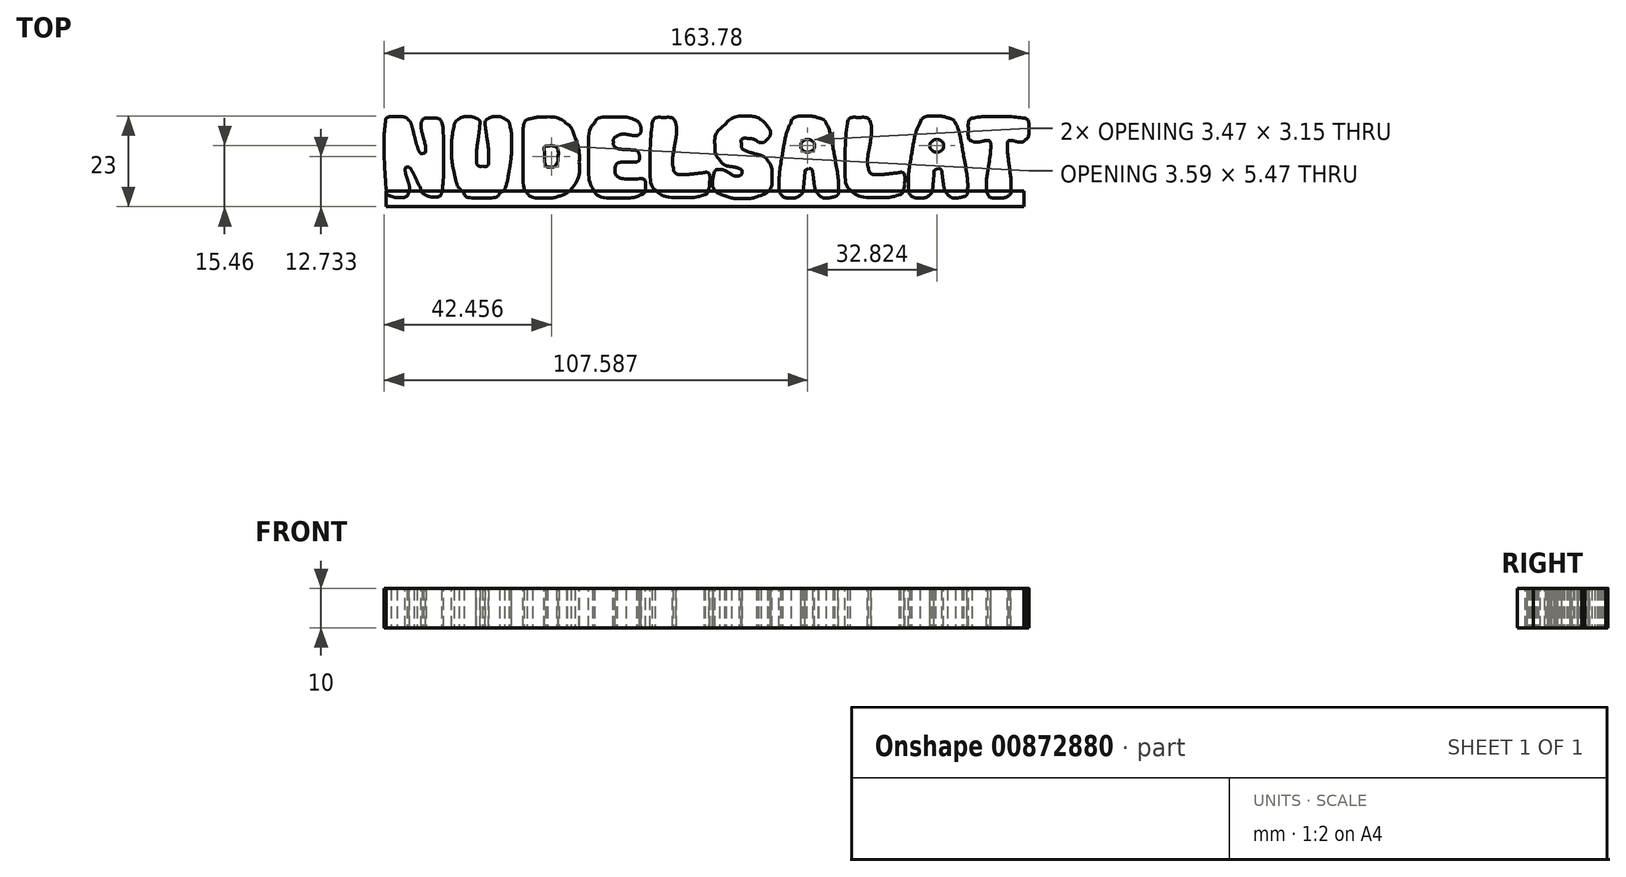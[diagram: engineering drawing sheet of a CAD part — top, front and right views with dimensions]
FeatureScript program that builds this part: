
annotation { "Feature Type Name" : "Feature", "Feature Type Description" : "" }
export const myFeature = defineFeature(function(context is Context, id is Id, definition is map)
    precondition{}
    {
        {
            var Q0;
            Q0=qCreatedBy(makeId("Top.planeOp"),FACE);
            var sketch = newSketch(context, id + "F0", { "sketchPlane" : qUnion([Q0])});
            skFitSpline(sketch, "E0", {"points": [v(-78.62, 10.37) * mm, v(-77.25, 10.37) * mm, v(-76.26, 10.07) * mm, v(-75.63, 9.46) * mm]});
            skFitSpline(sketch, "E1", {"points": [v(-75.63, 9.46) * mm, v(-75.27, 9.1) * mm, v(-74.9, 8.18) * mm, v(-74.52, 6.7) * mm]});
            skFitSpline(sketch, "E2", {"points": [v(-74.52, 6.7) * mm, v(-73.97, 4.47) * mm, v(-73.62, 3.19) * mm, v(-73.49, 2.85) * mm]});
            skFitSpline(sketch, "E3", {"points": [v(-73.49, 2.85) * mm, v(-73.03, 1.57) * mm, v(-72.51, 0.98) * mm, v(-71.92, 1.08) * mm]});
            skFitSpline(sketch, "E4", {"points": [v(-71.92, 1.08) * mm, v(-71.58, 1.13) * mm, v(-71.4, 1.47) * mm, v(-71.4, 2.08) * mm, v(-71.4, 2.78) * mm, v(-71.59, 3.82) * mm, v(-71.95, 5.18) * mm]});
            skFitSpline(sketch, "E5", {"points": [v(-71.95, 5.18) * mm, v(-72.31, 6.55) * mm, v(-72.5, 7.59) * mm, v(-72.5, 8.3) * mm, v(-72.5, 8.73) * mm, v(-72.42, 9.03) * mm, v(-72.26, 9.2) * mm]});
            skFitSpline(sketch, "E6", {"points": [v(-72.26, 9.2) * mm, v(-72.05, 9.72) * mm, v(-71.31, 9.97) * mm, v(-70.04, 9.97) * mm, v(-68.58, 9.97) * mm, v(-67.67, 9.67) * mm, v(-67.33, 9.06) * mm]});
            skFitSpline(sketch, "E7", {"points": [v(-67.33, 9.06) * mm, v(-67, 7.94) * mm, v(-66.84, 5.2) * mm, v(-66.84, 0.82) * mm, v(-66.84, -4.18) * mm, v(-67, -7.43) * mm, v(-67.33, -8.93) * mm]});
            skFitSpline(sketch, "E8", {"points": [v(-67.33, -8.93) * mm, v(-67.48, -9.65) * mm, v(-68.17, -10.02) * mm, v(-69.38, -10.02) * mm, v(-70.05, -10.02) * mm, v(-70.67, -9.87) * mm, v(-71.24, -9.59) * mm]});
            skFitSpline(sketch, "E9", {"points": [v(-71.24, -9.59) * mm, v(-71.9, -9.27) * mm, v(-72.31, -8.82) * mm, v(-72.46, -8.25) * mm]});
            skFitSpline(sketch, "E10", {"points": [v(-72.46, -8.25) * mm, v(-73.26, -6.6) * mm, v(-73.86, -5.36) * mm, v(-74.26, -4.54) * mm]});
            skFitSpline(sketch, "E11", {"points": [v(-74.26, -4.54) * mm, v(-74.93, -3.21) * mm, v(-75.53, -2.53) * mm, v(-76.08, -2.49) * mm]});
            skFitSpline(sketch, "E12", {"points": [v(-76.08, -2.49) * mm, v(-76.37, -2.53) * mm, v(-76.51, -2.75) * mm, v(-76.51, -3.17) * mm, v(-76.51, -3.69) * mm, v(-76.33, -4.5) * mm, v(-75.97, -5.61) * mm]});
            skFitSpline(sketch, "E13", {"points": [v(-75.97, -5.61) * mm, v(-75.6, -6.72) * mm, v(-75.43, -7.54) * mm, v(-75.43, -8.08) * mm, v(-75.43, -8.42) * mm, v(-75.5, -8.67) * mm, v(-75.66, -8.82) * mm]});
            skFitSpline(sketch, "E14", {"points": [v(-75.66, -8.82) * mm, v(-75.98, -9.71) * mm, v(-76.9, -10.16) * mm, v(-78.4, -10.16) * mm, v(-79, -10.16) * mm, v(-79.57, -10.05) * mm, v(-80.1, -9.84) * mm]});
            skFitSpline(sketch, "E15", {"points": [v(-80.1, -9.84) * mm, v(-80.8, -9.6) * mm, v(-81.2, -9.23) * mm, v(-81.3, -8.73) * mm]});
            skFitSpline(sketch, "E16", {"points": [v(-81.3, -8.73) * mm, v(-81.68, -3.87) * mm, v(-81.87, 0.03) * mm, v(-81.87, 2.96) * mm, v(-81.87, 5.4) * mm, v(-81.76, 7.4) * mm, v(-81.53, 8.98) * mm]});
            skFitSpline(sketch, "E17", {"points": [v(-81.53, 8.98) * mm, v(-81.4, 9.9) * mm, v(-80.43, 10.37) * mm, v(-78.62, 10.37) * mm]});
            skFitSpline(sketch, "E18", {"points": [v(-57.58, 8.33) * mm, v(-57.7, 7.1) * mm, v(-57.85, 5.76) * mm, v(-58.06, 4.28) * mm]});
            skFitSpline(sketch, "E19", {"points": [v(-58.06, 4.28) * mm, v(-58.3, 2.57) * mm, v(-58.43, 1.28) * mm, v(-58.43, 0.43) * mm, v(-58.43, -1.3) * mm, v(-57.92, -2.2) * mm, v(-56.9, -2.23) * mm]});
            skFitSpline(sketch, "E20", {"points": [v(-56.9, -2.23) * mm, v(-55.87, -2.27) * mm, v(-55.35, -1.32) * mm, v(-55.35, 0.61) * mm, v(-55.35, 1.56) * mm, v(-55.48, 2.88) * mm, v(-55.72, 4.57) * mm]});
            skFitSpline(sketch, "E21", {"points": [v(-55.72, 4.57) * mm, v(-56, 6.52) * mm, v(-56.17, 7.77) * mm, v(-56.2, 8.3) * mm]});
            skFitSpline(sketch, "E22", {"points": [v(-56.2, 8.3) * mm, v(-56.27, 9) * mm, v(-55.97, 9.54) * mm, v(-55.32, 9.92) * mm]});
            skFitSpline(sketch, "E23", {"points": [v(-55.32, 9.92) * mm, v(-54.8, 10.22) * mm, v(-54.15, 10.37) * mm, v(-53.41, 10.37) * mm, v(-52.6, 10.37) * mm, v(-51.87, 10.18) * mm, v(-51.25, 9.8) * mm]});
            skFitSpline(sketch, "E24", {"points": [v(-51.25, 9.8) * mm, v(-50.54, 9.39) * mm, v(-50.1, 8.8) * mm, v(-49.93, 8.04) * mm]});
            skFitSpline(sketch, "E25", {"points": [v(-49.93, 8.04) * mm, v(-49.63, 6.63) * mm, v(-49.48, 5) * mm, v(-49.48, 3.14) * mm, v(-49.48, 2.16) * mm, v(-49.53, 1.14) * mm, v(-49.64, 0.06) * mm]});
            skFitSpline(sketch, "E26", {"points": [v(-49.64, 0.06) * mm, v(-49.75, -1.02) * mm, v(-49.92, -2.15) * mm, v(-50.13, -3.32) * mm]});
            skFitSpline(sketch, "E27", {"points": [v(-50.13, -3.32) * mm, v(-50.7, -6.5) * mm, v(-51.5, -8.37) * mm, v(-52.5, -8.96) * mm]});
            skFitSpline(sketch, "E28", {"points": [v(-52.5, -8.96) * mm, v(-52.98, -9.84) * mm, v(-54.48, -10.27) * mm, v(-57, -10.27) * mm, v(-59.7, -10.27) * mm, v(-61.24, -9.8) * mm, v(-61.6, -8.88) * mm]});
            skFitSpline(sketch, "E29", {"points": [v(-61.6, -8.88) * mm, v(-62.76, -7.9) * mm, v(-63.6, -6.16) * mm, v(-64.14, -3.68) * mm]});
            skFitSpline(sketch, "E30", {"points": [v(-64.14, -3.68) * mm, v(-64.54, -1.87) * mm, v(-64.74, 0.11) * mm, v(-64.74, 2.25) * mm, v(-64.74, 4.13) * mm, v(-64.55, 5.98) * mm, v(-64.16, 7.82) * mm]});
            skFitSpline(sketch, "E31", {"points": [v(-64.16, 7.82) * mm, v(-63.97, 8.69) * mm, v(-63.55, 9.33) * mm, v(-62.88, 9.75) * mm]});
            skFitSpline(sketch, "E32", {"points": [v(-62.88, 9.75) * mm, v(-62.22, 10.17) * mm, v(-61.45, 10.37) * mm, v(-60.57, 10.37) * mm, v(-59.9, 10.37) * mm, v(-59.28, 10.25) * mm, v(-58.69, 10) * mm]});
            skFitSpline(sketch, "E33", {"points": [v(-58.69, 10) * mm, v(-57.93, 9.69) * mm, v(-57.55, 9.23) * mm, v(-57.55, 8.65) * mm, v(-57.55, 8.59) * mm, v(-57.56, 8.49) * mm, v(-57.58, 8.33) * mm]});
            skFitSpline(sketch, "E34", {"points": [v(-44.23, 9.95) * mm, v(-43.36, 10.17) * mm, v(-42.46, 10.29) * mm, v(-41.55, 10.29) * mm, v(-39.12, 10.29) * mm, v(-37.06, 9.69) * mm, v(-35.4, 8.5) * mm]});
            skFitSpline(sketch, "E35", {"points": [v(-35.4, 8.5) * mm, v(-34.7, 8) * mm, v(-34.04, 6.84) * mm, v(-33.4, 5.01) * mm]});
            skFitSpline(sketch, "E36", {"points": [v(-33.4, 5.01) * mm, v(-32.67, 2.98) * mm, v(-32.31, 0.92) * mm, v(-32.31, -1.15) * mm, v(-32.31, -3.92) * mm, v(-33, -6.23) * mm, v(-34.4, -8.08) * mm]});
            skFitSpline(sketch, "E37", {"points": [v(-34.4, -8.08) * mm, v(-34.68, -8.46) * mm, v(-35.07, -8.8) * mm, v(-35.58, -9.09) * mm]});
            skFitSpline(sketch, "E38", {"points": [v(-35.58, -9.09) * mm, v(-36.1, -9.38) * mm, v(-36.71, -9.64) * mm, v(-37.44, -9.84) * mm]});
            skFitSpline(sketch, "E39", {"points": [v(-37.44, -9.84) * mm, v(-38.6, -10.17) * mm, v(-39.8, -10.33) * mm, v(-41, -10.33) * mm, v(-43.2, -10.33) * mm, v(-44.73, -9.88) * mm, v(-45.6, -8.99) * mm]});
            skFitSpline(sketch, "E40", {"points": [v(-45.6, -8.99) * mm, v(-46.28, -8.02) * mm, v(-46.63, -4.08) * mm, v(-46.63, 2.82) * mm, v(-46.63, 6.07) * mm, v(-46.53, 8) * mm, v(-46.33, 8.6) * mm]});
            skFitSpline(sketch, "E41", {"points": [v(-46.33, 8.6) * mm, v(-46.13, 9.2) * mm, v(-45.43, 9.64) * mm, v(-44.23, 9.95) * mm]});
            skFitSpline(sketch, "E42", {"points": [v(-40.92, -1.75) * mm, v(-40.73, -2.24) * mm, v(-40.3, -2.49) * mm, v(-39.61, -2.49) * mm, v(-38.96, -2.49) * mm, v(-38.47, -2.22) * mm, v(-38.13, -1.69) * mm]});
            skFitSpline(sketch, "E43", {"points": [v(-38.13, -1.69) * mm, v(-37.84, -1.23) * mm, v(-37.7, -0.66) * mm, v(-37.7, 0.02) * mm, v(-37.7, 1.92) * mm, v(-38.6, 2.87) * mm, v(-40.4, 2.87) * mm]});
            skFitSpline(sketch, "E44", {"points": [v(-40.4, 2.87) * mm, v(-40.94, 2.87) * mm, v(-41.2, 2.58) * mm, v(-41.2, 1.99) * mm, v(-41.2, 1.76) * mm, v(-41.19, 1.42) * mm, v(-41.15, 0.96) * mm]});
            skFitSpline(sketch, "E45", {"points": [v(-41.15, 0.96) * mm, v(-41.11, 0.5) * mm, v(-41.1, 0.16) * mm, v(-41.1, -0.06) * mm, v(-41.1, -0.9) * mm, v(-41.04, -1.46) * mm, v(-40.92, -1.75) * mm]});
            skFitSpline(sketch, "E46", {"points": [v(-28.49, 8.78) * mm, v(-27.75, 9.78) * mm, v(-25.97, 10.29) * mm, v(-23.16, 10.29) * mm, v(-21.08, 10.29) * mm, v(-19.23, 9.95) * mm, v(-17.6, 9.26) * mm]});
            skFitSpline(sketch, "E47", {"points": [v(-17.6, 9.26) * mm, v(-16.99, 8.48) * mm, v(-16.68, 7.74) * mm, v(-16.68, 7.04) * mm, v(-16.68, 6.47) * mm, v(-16.9, 6.01) * mm, v(-17.34, 5.67) * mm]});
            skFitSpline(sketch, "E48", {"points": [v(-17.34, 5.67) * mm, v(-17.47, 5.57) * mm, v(-17.66, 5.53) * mm, v(-17.9, 5.53) * mm, v(-18.2, 5.53) * mm, v(-18.67, 5.59) * mm, v(-19.35, 5.71) * mm]});
            skFitSpline(sketch, "E49", {"points": [v(-19.35, 5.71) * mm, v(-20.02, 5.83) * mm, v(-20.53, 5.9) * mm, v(-20.87, 5.9) * mm, v(-21.6, 5.9) * mm, v(-22.22, 5.74) * mm, v(-22.76, 5.41) * mm]});
            skFitSpline(sketch, "E50", {"points": [v(-22.76, 5.41) * mm, v(-23.37, 5.03) * mm, v(-23.67, 4.5) * mm, v(-23.67, 3.82) * mm, v(-23.67, 3.2) * mm, v(-23.46, 2.79) * mm, v(-23.04, 2.56) * mm]});
            skFitSpline(sketch, "E51", {"points": [v(-23.04, 2.56) * mm, v(-22.66, 2.28) * mm, v(-21.8, 2.1) * mm, v(-20.45, 2.02) * mm]});
            skFitSpline(sketch, "E52", {"points": [v(-20.45, 2.02) * mm, v(-18.96, 1.92) * mm, v(-18.07, 1.83) * mm, v(-17.77, 1.73) * mm]});
            skFitSpline(sketch, "E53", {"points": [v(-17.77, 1.73) * mm, v(-17.53, 1.58) * mm, v(-17.35, 1.37) * mm, v(-17.23, 1.1) * mm]});
            skFitSpline(sketch, "E54", {"points": [v(-17.23, 1.1) * mm, v(-17.11, 0.83) * mm, v(-17.05, 0.5) * mm, v(-17.05, 0.1) * mm, v(-17.05, -0.48) * mm, v(-17.26, -0.9) * mm, v(-17.68, -1.15) * mm]});
            skFitSpline(sketch, "E55", {"points": [v(-20.4, -1.23) * mm, v(-21.82, -1.23) * mm, v(-22.73, -1.54) * mm, v(-23.13, -2.17) * mm]});
            skFitSpline(sketch, "E56", {"points": [v(-23.13, -2.17) * mm, v(-23.03, -4.4) * mm, v(-20.85, -5.46) * mm, v(-16.57, -5.37) * mm]});
            skFitSpline(sketch, "E57", {"points": [v(-16.57, -5.37) * mm, v(-15.85, -5.58) * mm, v(-15.48, -6.22) * mm, v(-15.48, -7.3) * mm, v(-15.48, -8.37) * mm, v(-15.95, -9.12) * mm, v(-16.88, -9.56) * mm]});
            skFitSpline(sketch, "E58", {"points": [v(-16.88, -9.56) * mm, v(-17.9, -10.04) * mm, v(-19.57, -10.27) * mm, v(-21.87, -10.27) * mm, v(-25.62, -10.27) * mm, v(-27.96, -9.44) * mm, v(-28.89, -7.76) * mm]});
            skFitSpline(sketch, "E59", {"points": [v(-28.89, -7.76) * mm, v(-29.61, -6.47) * mm, v(-29.97, -3.84) * mm, v(-29.97, 0.14) * mm, v(-29.97, 4.55) * mm, v(-29.48, 7.43) * mm, v(-28.49, 8.78) * mm]});
            skFitSpline(sketch, "E60", {"points": [v(-13.77, 8.75) * mm, v(-13.45, 9.7) * mm, v(-12.47, 10.17) * mm, v(-10.84, 10.17) * mm, v(-9.24, 10.17) * mm, v(-8.25, 9.76) * mm, v(-7.87, 8.92) * mm]});
            skFitSpline(sketch, "E61", {"points": [v(-7.87, 8.92) * mm, v(-7.72, 8.37) * mm, v(-7.64, 7.68) * mm, v(-7.64, 6.87) * mm, v(-7.64, 5.93) * mm, v(-7.8, 4.56) * mm, v(-8.13, 2.73) * mm]});
            skFitSpline(sketch, "E62", {"points": [v(-8.13, 2.73) * mm, v(-8.45, 0.9) * mm, v(-8.61, -0.46) * mm, v(-8.61, -1.38) * mm, v(-8.61, -1.8) * mm, v(-8.57, -2.12) * mm, v(-8.47, -2.34) * mm]});
            skFitSpline(sketch, "E63", {"points": [v(-8.47, -2.34) * mm, v(-8.17, -3.66) * mm, v(-7.03, -4.31) * mm, v(-5.08, -4.31) * mm, v(-4.58, -4.31) * mm, v(-3.81, -4.25) * mm, v(-2.77, -4.11) * mm]});
            skFitSpline(sketch, "E64", {"points": [v(-2.77, -4.11) * mm, v(-1.87, -4) * mm, v(-1.17, -3.92) * mm, v(-0.66, -3.88) * mm]});
            skFitSpline(sketch, "E65", {"points": [v(-0.66, -3.88) * mm, v(0.33, -3.8) * mm, v(0.83, -4.62) * mm, v(0.83, -6.3) * mm, v(0.83, -6.86) * mm, v(0.74, -7.44) * mm, v(0.57, -8.05) * mm]});
            skFitSpline(sketch, "E66", {"points": [v(0.57, -8.05) * mm, v(0.36, -8.83) * mm, v(0.07, -9.28) * mm, v(-0.31, -9.42) * mm]});
            skFitSpline(sketch, "E67", {"points": [v(-0.31, -9.42) * mm, v(-1.84, -9.91) * mm, v(-3.57, -10.16) * mm, v(-5.53, -10.16) * mm, v(-9, -10.16) * mm, v(-11.5, -9.5) * mm, v(-13.06, -8.16) * mm]});
            skFitSpline(sketch, "E68", {"points": [v(-13.06, -8.16) * mm, v(-13.9, -7.23) * mm, v(-14.32, -4.75) * mm, v(-14.32, -0.72) * mm, v(-14.32, 1.92) * mm, v(-14.14, 5.08) * mm, v(-13.77, 8.75) * mm]});
            skFitSpline(sketch, "E69", {"points": [v(16.23, 6.41) * mm, v(16.23, 5.82) * mm, v(15.96, 5.23) * mm, v(15.44, 4.64) * mm]});
            skFitSpline(sketch, "E70", {"points": [v(15.44, 4.64) * mm, v(14.92, 4.05) * mm, v(14.36, 3.76) * mm, v(13.77, 3.76) * mm, v(13.56, 3.76) * mm, v(13.36, 3.82) * mm, v(13.17, 3.93) * mm]});
            skFitSpline(sketch, "E71", {"points": [v(13.17, 3.93) * mm, v(12.17, 4.54) * mm, v(11.28, 4.84) * mm, v(10.52, 4.84) * mm, v(9.36, 4.84) * mm, v(8.82, 4.34) * mm, v(8.9, 3.33) * mm]});
            skFitSpline(sketch, "E72", {"points": [v(8.9, 3.33) * mm, v(8.95, 2.42) * mm, v(10.2, 1.6) * mm, v(12.66, 0.85) * mm]});
            skFitSpline(sketch, "E73", {"points": [v(12.66, 0.85) * mm, v(14.09, 0.43) * mm, v(15.1, -0.19) * mm, v(15.7, -1) * mm]});
            skFitSpline(sketch, "E74", {"points": [v(15.7, -1) * mm, v(16.3, -1.82) * mm, v(16.6, -2.97) * mm, v(16.6, -4.45) * mm, v(16.6, -7.04) * mm, v(15.48, -8.84) * mm, v(13.26, -9.84) * mm]});
            skFitSpline(sketch, "E75", {"points": [v(13.26, -9.84) * mm, v(11.99, -10.26) * mm, v(10.62, -10.47) * mm, v(9.15, -10.47) * mm, v(7.61, -10.47) * mm, v(6.2, -10.25) * mm, v(4.93, -9.82) * mm]});
            skFitSpline(sketch, "E76", {"points": [v(4.93, -9.82) * mm, v(3.35, -9.27) * mm, v(2.22, -8.45) * mm, v(1.54, -7.36) * mm]});
            skFitSpline(sketch, "E77", {"points": [v(1.54, -7.36) * mm, v(1.54, -6.26) * mm, v(1.6, -5.46) * mm, v(1.71, -4.97) * mm]});
            skFitSpline(sketch, "E78", {"points": [v(1.71, -4.97) * mm, v(2.01, -3.7) * mm, v(2.64, -3.06) * mm, v(3.6, -3.06) * mm, v(3.97, -3.06) * mm, v(4.65, -3.34) * mm, v(5.63, -3.9) * mm]});
            skFitSpline(sketch, "E79", {"points": [v(5.63, -3.9) * mm, v(6.61, -4.46) * mm, v(7.32, -4.74) * mm, v(7.76, -4.74) * mm, v(8.2, -4.74) * mm, v(8.6, -4.56) * mm, v(8.95, -4.2) * mm]});
            skFitSpline(sketch, "E80", {"points": [v(8.95, -4.2) * mm, v(9, -4.05) * mm, v(9.01, -3.91) * mm, v(9.01, -3.8) * mm, v(9.01, -3.36) * mm, v(8.75, -3.03) * mm, v(8.24, -2.8) * mm]});
            skFitSpline(sketch, "E81", {"points": [v(8.24, -2.8) * mm, v(7.92, -2.65) * mm, v(7.27, -2.49) * mm, v(6.3, -2.32) * mm]});
            skFitSpline(sketch, "E82", {"points": [v(6.3, -2.32) * mm, v(5.03, -2.09) * mm, v(4.02, -1.5) * mm, v(3.26, -0.55) * mm]});
            skFitSpline(sketch, "E83", {"points": [v(3.26, -0.55) * mm, v(2.51, 0.4) * mm, v(2.14, 1.53) * mm, v(2.14, 2.85) * mm, v(2.14, 4.94) * mm, v(2.95, 6.74) * mm, v(4.56, 8.26) * mm]});
            skFitSpline(sketch, "E84", {"points": [v(4.56, 8.26) * mm, v(6.14, 9.73) * mm, v(7.98, 10.46) * mm, v(10.1, 10.46) * mm, v(11.7, 10.46) * mm, v(12.95, 10.16) * mm, v(13.86, 9.55) * mm]});
            skFitSpline(sketch, "E85", {"points": [v(13.86, 9.55) * mm, v(14.43, 9.17) * mm, v(15.15, 8.38) * mm, v(16.03, 7.18) * mm]});
            skFitSpline(sketch, "E86", {"points": [v(16.03, 7.18) * mm, v(16.16, 6.95) * mm, v(16.23, 6.7) * mm, v(16.23, 6.41) * mm]});
            skFitSpline(sketch, "E87", {"points": [v(21.42, 8.78) * mm, v(21.95, 9.9) * mm, v(23.42, 10.46) * mm, v(25.84, 10.46) * mm, v(26.75, 10.46) * mm, v(27.6, 10.34) * mm, v(28.37, 10.09) * mm]});
            skFitSpline(sketch, "E88", {"points": [v(28.37, 10.09) * mm, v(29.42, 9.79) * mm, v(30.1, 9.32) * mm, v(30.4, 8.7) * mm]});
            skFitSpline(sketch, "E89", {"points": [v(30.4, 8.7) * mm, v(31.06, 7.38) * mm, v(31.76, 4.66) * mm, v(32.48, 0.52) * mm]});
            skFitSpline(sketch, "E90", {"points": [v(32.48, 0.52) * mm, v(33.18, -3.4) * mm, v(33.54, -6.25) * mm, v(33.54, -8.05) * mm, v(33.54, -8.87) * mm, v(33.45, -9.33) * mm, v(33.28, -9.45) * mm]});
            skFitSpline(sketch, "E91", {"points": [v(33.28, -9.45) * mm, v(33.15, -9.7) * mm, v(32.76, -9.9) * mm, v(32.11, -10.07) * mm]});
            skFitSpline(sketch, "E92", {"points": [v(32.11, -10.07) * mm, v(31.58, -10.2) * mm, v(31.12, -10.27) * mm, v(30.74, -10.27) * mm, v(29.83, -10.27) * mm, v(29.06, -10) * mm, v(28.43, -9.45) * mm]});
            skFitSpline(sketch, "E93", {"points": [v(28.43, -9.45) * mm, v(27.84, -8.5) * mm, v(27.48, -7.57) * mm, v(27.35, -6.66) * mm]});
            skFitSpline(sketch, "E94", {"points": [v(27.35, -6.66) * mm, v(27.31, -6.33) * mm, v(27.26, -5.92) * mm, v(27.2, -5.43) * mm]});
            skFitSpline(sketch, "E95", {"points": [v(27.2, -5.43) * mm, v(27.14, -4.94) * mm, v(27.06, -4.36) * mm, v(26.98, -3.71) * mm]});
            skFitSpline(sketch, "E96", {"points": [v(26.98, -3.71) * mm, v(26.84, -3.16) * mm, v(26.53, -2.89) * mm, v(26.04, -2.89) * mm, v(25.83, -2.89) * mm, v(25.6, -2.96) * mm, v(25.35, -3.1) * mm]});
            skFitSpline(sketch, "E97", {"points": [v(25.35, -3.1) * mm, v(25.1, -3.24) * mm, v(25, -3.42) * mm, v(25, -3.63) * mm]});
            skFitSpline(sketch, "E98", {"points": [v(25, -3.63) * mm, v(24.95, -4.43) * mm, v(24.85, -5.62) * mm, v(24.7, -7.2) * mm]});
            skFitSpline(sketch, "E99", {"points": [v(24.7, -7.2) * mm, v(24.58, -8.35) * mm, v(24.3, -9.11) * mm, v(23.87, -9.47) * mm]});
            skFitSpline(sketch, "E100", {"points": [v(23.87, -9.47) * mm, v(23.24, -10) * mm, v(22.45, -10.27) * mm, v(21.5, -10.27) * mm, v(20.25, -10.27) * mm, v(19.33, -9.9) * mm, v(18.76, -9.16) * mm]});
            skFitSpline(sketch, "E101", {"points": [v(18.76, -9.16) * mm, v(18.57, -8.99) * mm, v(18.48, -8.34) * mm, v(18.48, -7.22) * mm, v(18.48, -5.05) * mm, v(18.75, -2.4) * mm, v(19.28, 0.74) * mm]});
            skFitSpline(sketch, "E102", {"points": [v(19.28, 0.74) * mm, v(19.9, 4.4) * mm, v(20.62, 7.08) * mm, v(21.42, 8.78) * mm]});
            skFitSpline(sketch, "E103", {"points": [v(23.98, 2.96) * mm, v(23.98, 2.5) * mm, v(24.15, 2.13) * mm, v(24.5, 1.83) * mm]});
            skFitSpline(sketch, "E104", {"points": [v(24.5, 1.83) * mm, v(24.84, 1.54) * mm, v(25.24, 1.4) * mm, v(25.7, 1.4) * mm, v(26.15, 1.4) * mm, v(26.55, 1.54) * mm, v(26.9, 1.83) * mm]});
            skFitSpline(sketch, "E105", {"points": [v(26.9, 1.83) * mm, v(27.26, 2.13) * mm, v(27.43, 2.5) * mm, v(27.43, 2.96) * mm, v(27.43, 3.42) * mm, v(27.26, 3.8) * mm, v(26.9, 4.09) * mm]});
            skFitSpline(sketch, "E106", {"points": [v(26.9, 4.09) * mm, v(26.55, 4.38) * mm, v(26.15, 4.53) * mm, v(25.7, 4.53) * mm, v(25.24, 4.53) * mm, v(24.84, 4.38) * mm, v(24.5, 4.09) * mm]});
            skFitSpline(sketch, "E107", {"points": [v(24.5, 4.09) * mm, v(24.15, 3.8) * mm, v(23.98, 3.42) * mm, v(23.98, 2.96) * mm]});
            skFitSpline(sketch, "E108", {"points": [v(35.76, 8.75) * mm, v(36.08, 9.7) * mm, v(37.06, 10.17) * mm, v(38.7, 10.17) * mm, v(40.3, 10.17) * mm, v(41.28, 9.76) * mm, v(41.66, 8.92) * mm]});
            skFitSpline(sketch, "E109", {"points": [v(41.66, 8.92) * mm, v(41.82, 8.37) * mm, v(41.9, 7.68) * mm, v(41.9, 6.87) * mm, v(41.9, 5.93) * mm, v(41.73, 4.56) * mm, v(41.4, 2.73) * mm]});
            skFitSpline(sketch, "E110", {"points": [v(41.4, 2.73) * mm, v(41.08, 0.9) * mm, v(40.92, -0.46) * mm, v(40.92, -1.38) * mm, v(40.92, -1.8) * mm, v(40.97, -2.12) * mm, v(41.07, -2.34) * mm]});
            skFitSpline(sketch, "E111", {"points": [v(41.07, -2.34) * mm, v(41.37, -3.66) * mm, v(42.5, -4.31) * mm, v(44.46, -4.31) * mm, v(44.95, -4.31) * mm, v(45.72, -4.25) * mm, v(46.77, -4.11) * mm]});
            skFitSpline(sketch, "E112", {"points": [v(46.77, -4.11) * mm, v(47.66, -4) * mm, v(48.37, -3.92) * mm, v(48.88, -3.88) * mm]});
            skFitSpline(sketch, "E113", {"points": [v(48.88, -3.88) * mm, v(49.87, -3.8) * mm, v(50.36, -4.62) * mm, v(50.36, -6.3) * mm, v(50.36, -6.86) * mm, v(50.28, -7.44) * mm, v(50.1, -8.05) * mm]});
            skFitSpline(sketch, "E114", {"points": [v(50.1, -8.05) * mm, v(49.9, -8.83) * mm, v(49.6, -9.28) * mm, v(49.22, -9.42) * mm]});
            skFitSpline(sketch, "E115", {"points": [v(49.22, -9.42) * mm, v(47.7, -9.91) * mm, v(45.96, -10.16) * mm, v(44, -10.16) * mm, v(40.54, -10.16) * mm, v(38.03, -9.5) * mm, v(36.47, -8.16) * mm]});
            skFitSpline(sketch, "E116", {"points": [v(36.47, -8.16) * mm, v(35.64, -7.23) * mm, v(35.22, -4.75) * mm, v(35.22, -0.72) * mm, v(35.22, 1.92) * mm, v(35.4, 5.08) * mm, v(35.76, 8.75) * mm]});
            skFitSpline(sketch, "E117", {"points": [v(54.24, 8.78) * mm, v(54.77, 9.9) * mm, v(56.25, 10.46) * mm, v(58.66, 10.46) * mm, v(59.57, 10.46) * mm, v(60.42, 10.34) * mm, v(61.2, 10.09) * mm]});
            skFitSpline(sketch, "E118", {"points": [v(61.2, 10.09) * mm, v(62.24, 9.79) * mm, v(62.92, 9.32) * mm, v(63.22, 8.7) * mm]});
            skFitSpline(sketch, "E119", {"points": [v(63.22, 8.7) * mm, v(63.89, 7.38) * mm, v(64.58, 4.66) * mm, v(65.3, 0.52) * mm]});
            skFitSpline(sketch, "E120", {"points": [v(65.3, 0.52) * mm, v(66, -3.4) * mm, v(66.36, -6.25) * mm, v(66.36, -8.05) * mm, v(66.36, -8.87) * mm, v(66.27, -9.33) * mm, v(66.1, -9.45) * mm]});
            skFitSpline(sketch, "E121", {"points": [v(66.1, -9.45) * mm, v(65.97, -9.7) * mm, v(65.58, -9.9) * mm, v(64.93, -10.07) * mm]});
            skFitSpline(sketch, "E122", {"points": [v(64.93, -10.07) * mm, v(64.4, -10.2) * mm, v(63.95, -10.27) * mm, v(63.57, -10.27) * mm, v(62.65, -10.27) * mm, v(61.88, -10) * mm, v(61.26, -9.45) * mm]});
            skFitSpline(sketch, "E123", {"points": [v(61.26, -9.45) * mm, v(60.67, -8.5) * mm, v(60.3, -7.57) * mm, v(60.17, -6.66) * mm]});
            skFitSpline(sketch, "E124", {"points": [v(60.17, -6.66) * mm, v(60.13, -6.33) * mm, v(60.08, -5.92) * mm, v(60.02, -5.43) * mm]});
            skFitSpline(sketch, "E125", {"points": [v(60.02, -5.43) * mm, v(59.96, -4.94) * mm, v(59.89, -4.36) * mm, v(59.8, -3.71) * mm]});
            skFitSpline(sketch, "E126", {"points": [v(59.8, -3.71) * mm, v(59.67, -3.16) * mm, v(59.35, -2.89) * mm, v(58.86, -2.89) * mm, v(58.65, -2.89) * mm, v(58.42, -2.96) * mm, v(58.18, -3.1) * mm]});
            skFitSpline(sketch, "E127", {"points": [v(58.18, -3.1) * mm, v(57.93, -3.24) * mm, v(57.81, -3.42) * mm, v(57.83, -3.63) * mm]});
            skFitSpline(sketch, "E128", {"points": [v(57.83, -3.63) * mm, v(57.78, -4.43) * mm, v(57.67, -5.62) * mm, v(57.52, -7.2) * mm]});
            skFitSpline(sketch, "E129", {"points": [v(57.52, -7.2) * mm, v(57.4, -8.35) * mm, v(57.13, -9.11) * mm, v(56.7, -9.47) * mm]});
            skFitSpline(sketch, "E130", {"points": [v(56.7, -9.47) * mm, v(56.07, -10) * mm, v(55.28, -10.27) * mm, v(54.33, -10.27) * mm, v(53.07, -10.27) * mm, v(52.16, -9.9) * mm, v(51.59, -9.16) * mm]});
            skFitSpline(sketch, "E131", {"points": [v(51.59, -9.16) * mm, v(51.4, -8.99) * mm, v(51.3, -8.34) * mm, v(51.3, -7.22) * mm, v(51.3, -5.05) * mm, v(51.57, -2.4) * mm, v(52.1, 0.74) * mm]});
            skFitSpline(sketch, "E132", {"points": [v(52.1, 0.74) * mm, v(52.73, 4.4) * mm, v(53.44, 7.08) * mm, v(54.24, 8.78) * mm]});
            skFitSpline(sketch, "E133", {"points": [v(56.8, 2.96) * mm, v(56.8, 2.5) * mm, v(56.98, 2.13) * mm, v(57.32, 1.83) * mm]});
            skFitSpline(sketch, "E134", {"points": [v(57.32, 1.83) * mm, v(57.66, 1.54) * mm, v(58.06, 1.4) * mm, v(58.52, 1.4) * mm, v(58.97, 1.4) * mm, v(59.38, 1.54) * mm, v(59.73, 1.83) * mm]});
            skFitSpline(sketch, "E135", {"points": [v(59.73, 1.83) * mm, v(60.08, 2.13) * mm, v(60.26, 2.5) * mm, v(60.26, 2.96) * mm, v(60.26, 3.42) * mm, v(60.08, 3.8) * mm, v(59.73, 4.09) * mm]});
            skFitSpline(sketch, "E136", {"points": [v(59.73, 4.09) * mm, v(59.38, 4.38) * mm, v(58.97, 4.53) * mm, v(58.52, 4.53) * mm, v(58.06, 4.53) * mm, v(57.66, 4.38) * mm, v(57.32, 4.09) * mm]});
            skFitSpline(sketch, "E137", {"points": [v(57.32, 4.09) * mm, v(56.98, 3.8) * mm, v(56.8, 3.42) * mm, v(56.8, 2.96) * mm]});
            skFitSpline(sketch, "E138", {"points": [v(67.44, 9.95) * mm, v(69.02, 10.23) * mm, v(71.2, 10.37) * mm, v(74, 10.37) * mm, v(76.57, 10.37) * mm, v(78.86, 10.23) * mm, v(80.88, 9.95) * mm]});
            skFitSpline(sketch, "E139", {"points": [v(80.88, 9.95) * mm, v(81.54, 9.65) * mm, v(81.87, 8.7) * mm, v(81.87, 7.14) * mm, v(81.87, 5.72) * mm, v(81.6, 4.87) * mm, v(81.05, 4.58) * mm]});
            skFitSpline(sketch, "E140", {"points": [v(81.05, 4.58) * mm, v(80.69, 4.13) * mm, v(80.22, 3.9) * mm, v(79.65, 3.9) * mm, v(79.36, 3.9) * mm, v(78.95, 3.97) * mm, v(78.4, 4.11) * mm]});
            skFitSpline(sketch, "E141", {"points": [v(78.4, 4.11) * mm, v(77.84, 4.26) * mm, v(77.44, 4.33) * mm, v(77.2, 4.33) * mm, v(76.91, 4.33) * mm, v(76.7, 4.22) * mm, v(76.57, 4.02) * mm]});
            skFitSpline(sketch, "E142", {"points": [v(76.57, 4.02) * mm, v(76.5, 3.9) * mm, v(76.46, 3.65) * mm, v(76.46, 3.25) * mm, v(76.46, 2.04) * mm, v(76.61, 0.23) * mm, v(76.93, -2.2) * mm]});
            skFitSpline(sketch, "E143", {"points": [v(76.93, -2.2) * mm, v(77.24, -4.61) * mm, v(77.4, -6.43) * mm, v(77.4, -7.64) * mm, v(77.4, -8.66) * mm, v(77.28, -9.25) * mm, v(77.05, -9.42) * mm]});
            skFitSpline(sketch, "E144", {"points": [v(77.05, -9.42) * mm, v(76.31, -9.99) * mm, v(75.26, -10.27) * mm, v(73.89, -10.27) * mm, v(72.58, -10.27) * mm, v(71.75, -9.9) * mm, v(71.4, -9.16) * mm]});
            skFitSpline(sketch, "E145", {"points": [v(71.4, -9.16) * mm, v(71.2, -8.95) * mm, v(71.1, -8.4) * mm, v(71.1, -7.48) * mm, v(71.1, -6.29) * mm, v(71.28, -4.5) * mm, v(71.65, -2.12) * mm]});
            skFitSpline(sketch, "E146", {"points": [v(71.65, -2.12) * mm, v(72.02, 0.26) * mm, v(72.2, 2.05) * mm, v(72.2, 3.25) * mm, v(72.2, 3.63) * mm, v(72.17, 3.84) * mm, v(72.1, 3.9) * mm]});
            skFitSpline(sketch, "E147", {"points": [v(72.1, 3.9) * mm, v(71.96, 4.19) * mm, v(71.72, 4.33) * mm, v(71.38, 4.33) * mm, v(71.11, 4.33) * mm, v(70.68, 4.25) * mm, v(70.07, 4.1) * mm]});
            skFitSpline(sketch, "E148", {"points": [v(70.07, 4.1) * mm, v(69.46, 3.95) * mm, v(69, 3.87) * mm, v(68.67, 3.87) * mm, v(68.21, 3.87) * mm, v(67.8, 3.97) * mm, v(67.44, 4.16) * mm]});
            skFitSpline(sketch, "E149", {"points": [v(67.44, 4.16) * mm, v(66.82, 4.48) * mm, v(66.5, 5.43) * mm, v(66.5, 7.02) * mm, v(66.5, 8.6) * mm, v(66.82, 9.57) * mm, v(67.44, 9.95) * mm]});
            skLineSegment(sketch, "E150", {"start": v(-20.4, -1.23) * mm, "end": v(-17.68, -1.15) * mm});
            skSolve(sketch);
        }
        {
            var Q0;
            Q0 = qSketchRegion(id + "F0", true);
            extrude(context, id + "F1", {"entities" : qUnion([Q0]), "depth" : 10 * mm, "offsetDistance" : 25 * mm});
        }
        {
            var Q0;
            Q0=qCreatedBy(makeId("Top.planeOp"),FACE);
            var sketch = newSketch(context, id + "F2", { "sketchPlane" : qUnion([Q0])});
            skLineSegment(sketch, "E151.bottom", {"start": v(-81.4, -8.5) * mm, "end": v(80.6, -8.5) * mm});
            skLineSegment(sketch, "E151.top", {"start": v(-81.4, -12.5) * mm, "end": v(80.6, -12.5) * mm});
            skLineSegment(sketch, "E151.left", {"start": v(-81.4, -8.5) * mm, "end": v(-81.4, -12.5) * mm});
            skLineSegment(sketch, "E151.right", {"start": v(80.6, -8.5) * mm, "end": v(80.6, -12.5) * mm});
            skSolve(sketch);
        }
        {
            var Q0;
            Q0 = qSketchRegion(id + "F2", true);
            extrude(context, id + "F3", {"entities" : qUnion([Q0]), "depth" : 10 * mm, "offsetDistance" : 25 * mm});
        }
    });
